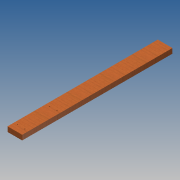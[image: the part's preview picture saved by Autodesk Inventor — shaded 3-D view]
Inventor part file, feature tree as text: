
AUTODESK INVENTOR PART (.ipt)
format: ipt  version: 2014 SP1 (Build 180222100, 222)  size: 90,624 bytes
history: native  units: in
note: dims shown in document units (in); Inventor stores cm internally (conversion verified against a paired STEP export)
features: sketch x2, extrude x1, hole x1
ambient origin geometry x8: Origin, YZ Plane, XZ Plane, XY Plane, X Axis, Y Axis, Z Axis, Center Point
bodies: Solid1 (feature_tree)
feature tree (4):
  extrude  "Extrusion1"  Depth=46.0in
  hole  "Hole3"  [1 undecoded]
  sketch  "Sketch1"  dims[d0=1.4961in d1=46.0in]
  sketch  "Sketch4"  dims[d3=90.0deg d4=4.4882in d5=0.0in d46=1.122in d47=0.7874in d49=2.2441in d50=0.7874in d52=9.8425in d55=0.266in d56=0.75in d57=0.507in d58=0.25in d59=0.5635in d60=1.0in d61=0.8108in]
note: 1 required parameter value undecoded (feature->parameter linkage not recoverable at this tier; creation-order binding heuristic only, values carry confidence <= 0.55)
